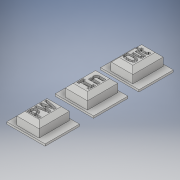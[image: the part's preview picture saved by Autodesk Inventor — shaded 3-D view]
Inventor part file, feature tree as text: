
AUTODESK INVENTOR PART (.ipt)
format: ipt  version: 2019 (Build 230136000, 136)  size: 586,752 bytes
history: native  units: mm
features: move_body x29, sketch x4, direct_edit x4, delete_face x4, extrude x3, other x2, chamfer x2, imported_body x2
ambient origin geometry x8: Origin, YZ Plane, XZ Plane, XY Plane, X Axis, Y Axis, Z Axis, Center Point
bodies: Solid1 (feature_tree), Solid2 (feature_tree), Solid3 (feature_tree)
feature tree (50):
  other  "Repaired Geometry1"
  other  "Repaired Geometry2"
  extrude  "Extrusion1"  Depth=6.0mm
  sketch  "Sketch2"  dims[d2=2.0mm d3=0.0mm d4=7.0mm]
  extrude  "Extrusion2"  Depth=7.0mm
  move_body  "Move Body1"
  move_body  "Move Body2"
  move_body  "Move Body3"
  move_body  "Move Body4"
  move_body  "Move Body5"
  move_body  "Move Body6"
  extrude  "Extrusion3"  Depth=0.5mm TaperAngle=0.0deg
  direct_edit  "Direct Edit1"
  chamfer  "Chamfer1"  [1 undecoded]
  delete_face  "Delete Face1"
  delete_face  "Delete Face2"
  delete_face  "Delete Face3"
  delete_face  "Delete Face4"
  direct_edit  "Direct Edit2"
  move_body  "Move Body7"
  move_body  "Move Body8"
  direct_edit  "Direct Edit3"
  chamfer  "Chamfer2"  Distance=10.0mm
  direct_edit  "Direct Edit4"
  sketch  "Sketch1"  dims[d0=4.0mm d1=6.0mm]
  sketch  "Sketch3"  dims[d5=7.0mm d6=0.5mm d7=0.0mm d8=0.0mm d9=0.0mm d10=-7.5mm d11=10.0mm d12=0.0mm d13=0.0mm]
  imported_body  "Base1"
  imported_body  "Base2"
  sketch  "Sketch4"  dims[d14=-10.25mm d15=0.0mm d16=8.75mm d17=-10.25mm d18=0.0mm d19=0.5mm d20=10.0mm d21=0.0mm d22=0.0mm d23=-10.25mm d24=0.0mm d25=0.0mm d26=0.6mm d27=0.0mm d28=0.0mm d29=0.0mm d30=1.0mm d31=0.0mm d32=0.0mm d33=1.0mm d34=0.0mm d35=0.0mm d36=1.0mm d37=0.4mm d38=2.0mm d39=45.0deg d40=0.0mm d41=0.0mm d42=0.75mm d43=0.0mm d44=0.0mm d45=0.75mm d46=0.0mm d47=0.0mm d48=0.75mm d49=0.0mm d50=0.0mm d51=0.75mm d52=0.0mm d53=0.0mm d54=3.75mm d55=0.0mm d56=0.0mm d57=-3.25mm d58=0.75mm d59=0.0mm d60=0.0mm d61=0.0mm d62=0.0mm d63=0.75mm d64=0.0mm d65=0.0mm d66=0.75mm d67=0.0mm d68=0.0mm d69=0.75mm d70=0.0mm d71=0.0mm d72=0.75mm d73=0.0mm d74=0.0mm d75=0.75mm d76=0.0mm d77=0.0mm d78=0.75mm d79=0.0mm d80=0.0mm d81=0.75mm d82=1.0mm d83=2.0mm d84=45.0deg d85=0.0mm d86=0.0mm d87=0.5mm d88=0.0mm d89=0.0mm d90=0.5mm d91=0.0mm d92=0.0mm d93=0.5mm d94=0.0mm d95=0.0mm d96=0.5mm d97=0.0mm d98=0.0mm d99=0.5mm d100=0.0mm d101=0.0mm d102=0.5mm]
  move_body  "Move1"
  move_body  "Move2"
  move_body  "Move3"
  move_body  "Move4"
  move_body  "Move5"
  move_body  "Move6"
  move_body  "Move7"
  move_body  "Move8"
  move_body  "Move9"
  move_body  "Move10"
  move_body  "Move11"
  move_body  "Move12"
  move_body  "Move13"
  move_body  "Move14"
  move_body  "Move15"
  move_body  "Move16"
  move_body  "Move17"
  move_body  "Move18"
  move_body  "Move19"
  move_body  "Move20"
  move_body  "Move21"
note: 1 required parameter value undecoded (feature->parameter linkage not recoverable at this tier; creation-order binding heuristic only, values carry confidence <= 0.55)
